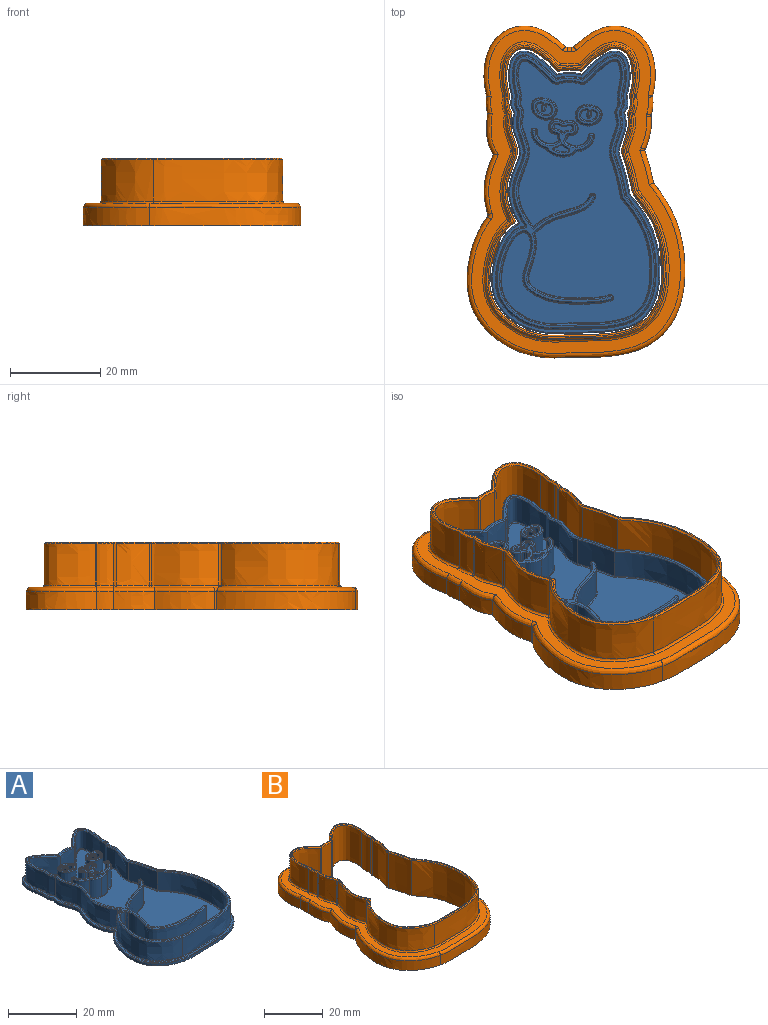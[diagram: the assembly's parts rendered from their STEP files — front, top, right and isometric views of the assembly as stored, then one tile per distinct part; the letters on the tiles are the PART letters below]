
ASSEMBLY  parts=2 mates=1
PART A: 278 faces, bbox 38x64x8.3 mm
  f0: plane 58.1x32.85mm, normal (0,0,1), area 1171.6mm2, adj f142,f143,f144,f146,f147,f148,f149,f150
  f1: plane 62.1x36.86mm, normal (0,0,1), area 109.3mm2, adj f176,f177,f178,f179,f180,f181,f182,f183
  f2: extruded ~24.09x2.39mm, area 20.1mm2, adj f9,f10,f101,f182
  f3: extruded ~23.81x10.4mm, area 24.8mm2, adj f4,f10,f101,f183
  f4: extruded ~30.82x26.84mm, area 43.2mm2, adj f3,f5,f10,f181
  f5: extruded ~8.83x2.36mm, area 7.3mm2, adj f4,f6,f10,f179
  f6: extruded ~9.18x1.59mm, area 7.6mm2, adj f5,f7,f10,f177
  f7: extruded ~13.63x10.73mm, area 19.6mm2, adj f6,f8,f10,f176
  f8: extruded ~5.46x0.8mm, area 4.4mm2, adj f7,f9,f10,f178
  f9: extruded ~13.63x10.73mm, area 19.6mm2, adj f2,f8,f10,f180
  f10: plane 62.5x37.25mm, normal (0,0,-1), area 1734.6mm2, adj f2,f3,f4,f5,f6,f7,f8,f9
  f11: extruded ~6.55x0.43mm, area 2.8mm2, adj f12,f96,f138,f214
  f12: extruded ~22.13x9.63mm, area 191.2mm2, adj f11,f13,f136,f212
  f13: extruded ~29.37x25.61mm, area 339.5mm2, adj f12,f14,f134,f210
  f14: extruded ~9.01x6.55mm, area 61.1mm2, adj f13,f15,f132,f208
  f15: extruded ~9.62x6.55mm, area 64.9mm2, adj f14,f16,f131,f206
  f16: extruded ~12.49x9.58mm, area 148.7mm2, adj f15,f17,f133,f207
  f17: extruded ~6.55x5.73mm, area 38.2mm2, adj f16,f18,f135,f209
  f18: extruded ~12.56x9.59mm, area 149mm2, adj f17,f19,f137,f211
  f19: extruded ~24.41x6.55mm, area 167.4mm2, adj f18,f36,f139,f213
  f20: extruded ~12.65x7.14mm, area 97.7mm2, adj f21,f94,f130,f199
  f21: extruded ~6.55x0.78mm, area 6.5mm2, adj f20,f22,f128,f197
  f22: extruded ~36.26x8.57mm, area 311.2mm2, adj f21,f23,f126,f195
  f23: extruded ~6.55x5.73mm, area 38.3mm2, adj f22,f24,f124,f193
  f24: extruded ~21.35x8.57mm, area 206.4mm2, adj f23,f25,f122,f191
  f25: extruded ~9.19x6.55mm, area 62.3mm2, adj f24,f26,f120,f189
  f26: extruded ~27.91x24.38mm, area 324.8mm2, adj f25,f27,f118,f187
  f27: extruded ~20.21x8.86mm, area 181.9mm2, adj f26,f28,f116,f185
  f28: extruded ~6.55x0.93mm, area 7.1mm2, adj f27,f29,f114,f186
  f29: extruded ~19.53x14.59mm, area 205mm2, adj f28,f93,f112,f188
  f30: plane 6.55x0.17mm, normal (0.64,0.77,0), area 1.4mm2, adj f92,f93,f111,f192
  f31: extruded ~18.01x14.07mm, area 194.5mm2, adj f32,f92,f115,f196
  f32: extruded ~6.55x0.13mm, area 0.9mm2, adj f31,f91,f117,f198
  f33: extruded ~6.55x0.42mm, area 3.8mm2, adj f34,f91,f121,f202
  f34: extruded ~12.92x7.56mm, area 101mm2, adj f33,f95,f123,f204
  f35: plane 6.55x0.19mm, normal (0.27,0.96,0), area 1.3mm2, adj f94,f95,f127,f203
  f36: extruded ~6.55x0.37mm, area 3mm2, adj f19,f96,f141,f215
  f37: plane 60.43x35.28mm, normal (0,0,1), area 95.6mm2, adj f110,f111,f112,f113,f114,f115,f116,f117
  f38: extruded ~6.75x1.42mm, area 20.1mm2, adj f39,f77,f80,f229
  f39: extruded ~6.75x1.1mm, area 8.2mm2, adj f38,f40,f80,f231
  f40: extruded ~6.75x0.18mm, area 1.7mm2, adj f39,f41,f80,f233
  f41: extruded ~6.75x0.25mm, area 2mm2, adj f40,f42,f80,f234
  f42: extruded ~6.75x1.03mm, area 8.2mm2, adj f41,f43,f80,f232
  f43: extruded ~6.75x1.32mm, area 18.5mm2, adj f42,f44,f80,f230
  f44: extruded ~6.75x0.51mm, area 3.7mm2, adj f43,f45,f80,f228
  f45: extruded ~6.75x0.28mm, area 1.9mm2, adj f44,f46,f80,f226
  f46: extruded ~6.75x0.24mm, area 1.6mm2, adj f45,f77,f80,f225
  f47: extruded ~6.5x3.33mm, area 29.5mm2, adj f48,f97,f172,f270
  f48: extruded ~6.5x1.96mm, area 14.8mm2, adj f47,f108,f174,f268
  f49: extruded ~6.5x0.39mm, area 2.9mm2, adj f50,f108,f173,f264
  f50: extruded ~6.5x0.44mm, area 3.1mm2, adj f49,f51,f171,f262
  f51: plane 6.5x0.02mm, normal (0.97,-0.26,0), area 0.2mm2, adj f50,f52,f169
  f52: extruded ~6.5x0.39mm, area 3.3mm2, adj f51,f53,f167,f259
  f53: extruded ~6.5x0.01mm, area 0.1mm2, adj f52,f164,f245
  f54: extruded ~6.5x0.09mm, area 0.6mm2, adj f55,f165,f245,f255
  f55: extruded ~6.5x3.08mm, area 39.8mm2, adj f54,f56,f162,f253
  f56: extruded ~6.5x0.31mm, area 2.1mm2, adj f55,f57,f160,f251
  f57: extruded ~6.5x0.34mm, area 2.3mm2, adj f56,f58,f154,f156,f158,f249
  f58: extruded ~6.5x0.47mm, area 3.4mm2, adj f57,f59,f152,f248
  f59: extruded ~6.5x3.01mm, area 35.7mm2, adj f58,f60,f150,f250
  f60: extruded ~6.5x0.48mm, area 3.2mm2, adj f59,f61,f148,f252
  f61: extruded ~6.5x0.47mm, area 3.9mm2, adj f60,f62,f146,f254
  f62: plane 6.5x0.02mm, normal (-1,-0.05,0), area 0.1mm2, adj f61,f63,f144
  f63: extruded ~6.5x0.46mm, area 3mm2, adj f62,f64,f142,f257
  f64: extruded ~6.5x0.42mm, area 2.9mm2, adj f63,f109,f143,f258
  f65: extruded ~6.5x2.11mm, area 14.8mm2, adj f66,f109,f147,f261
  f66: extruded ~6.5x2.89mm, area 29.5mm2, adj f65,f100,f149,f263
  f67: plane 6.5x0.2mm, normal (0.16,0.99,0), area 1.3mm2, adj f99,f100,f153,f267
  f68: extruded ~6.5x3.91mm, area 35.9mm2, adj f69,f99,f157,f271
  f69: extruded ~6.5x3.21mm, area 24.6mm2, adj f68,f70,f159,f273
  f70: extruded ~6.5x3.46mm, area 24.6mm2, adj f69,f71,f161,f275
  f71: extruded ~6.5x3.81mm, area 35.9mm2, adj f70,f98,f163,f277
  f72: extruded ~6.75x1.4mm, area 12mm2, adj f76,f79,f106,f222
  f73: extruded ~6.75x1.51mm, area 10.3mm2, adj f74,f79,f106,f219
  f74: extruded ~6.75x1.47mm, area 10.3mm2, adj f73,f79,f107,f221
  f75: plane 6.5x0.2mm, normal (0.02,1,0), area 1.3mm2, adj f97,f98,f168,f274
  f76: extruded ~6.75x1.56mm, area 12mm2, adj f72,f79,f107,f224
  f77: extruded ~6.75x0.41mm, area 2.8mm2, adj f38,f46,f80,f227
  f78: plane 13.32x7.75mm, normal (0,0,1), area 17.7mm2, adj f219,f220,f221,f222,f223,f224,f225,f226
  f79: plane 3.24x1.59mm, normal (0,0,1), area 2.9mm2, adj f72,f73,f74,f76,f106,f107
  f80: plane 4.21x1.97mm, normal (0,0,1), area 4.2mm2, adj f38,f39,f40,f41,f42,f43,f44,f45
  f81: extruded ~6.75x3.56mm, area 55.2mm2, adj f85,f104,f105,f241
  f82: extruded ~6.55x5.53mm, area 102.5mm2, adj f218,f244
  f83: extruded ~6.75x1.59mm, area 24.3mm2, adj f85,f104,f105,f242
  f84: plane 5.33x4.14mm, normal (0,0,1), area 7.4mm2, adj f240,f241,f242,f243,f244
  f85: plane 3.64x2.43mm, normal (0,0,1), area 5mm2, adj f81,f83,f104,f105
  f86: extruded ~6.75x3.38mm, area 55.2mm2, adj f90,f102,f103,f237
  f87: extruded ~6.75x1.63mm, area 24.3mm2, adj f90,f102,f103,f236
  f88: extruded ~6.55x5.36mm, area 102.5mm2, adj f217,f239
  f89: plane 5.11x4.28mm, normal (0,0,1), area 7.1mm2, adj f235,f236,f237,f238,f239
  f90: plane 3.46x2.64mm, normal (0,0,1), area 5mm2, adj f86,f87,f102,f103
  f91: cylinder r=0.4mm len=6.55mm, axis (0,0,-1), area 3mm2, adj f32,f33,f119,f200
  f92: cylinder r=0.4mm len=6.55mm, axis (0,0,-1), area 2.9mm2, adj f30,f31,f113,f194
  f93: cylinder r=0.4mm len=6.55mm, axis (0,0,-1), area 5.2mm2, adj f29,f30,f110,f190
  f94: cylinder r=0.4mm len=6.55mm, axis (0,0,-1), area 3.9mm2, adj f20,f35,f129,f201
  f95: cylinder r=0.4mm len=6.55mm, axis (0,0,-1), area 4.3mm2, adj f34,f35,f125,f205
  f96: cylinder r=0.4mm len=6.55mm, axis (0,0,-1), area 5.6mm2, adj f11,f36,f140,f216
  f97: cylinder r=0.4mm len=6.5mm, axis (0,0,-1), area 3.9mm2, adj f47,f75,f170,f272
  f98: cylinder r=0.4mm len=6.5mm, axis (0,0,-1), area 4.2mm2, adj f71,f75,f166,f276
  f99: cylinder r=0.4mm len=6.5mm, axis (0,0,-1), area 4.2mm2, adj f67,f68,f155,f269
  f100: cylinder r=0.4mm len=6.5mm, axis (0,0,-1), area 3.9mm2, adj f66,f67,f151,f265
  f101: cylinder r=0.4mm len=0.8mm, axis (0,0,-1), area 0.5mm2, adj f2,f3,f10,f184
  f102: cylinder r=0.2mm len=6.75mm, axis (0,0,-1), area 2.9mm2, adj f86,f87,f90,f235
  f103: cylinder r=0.2mm len=6.75mm, axis (0,0,-1), area 3mm2, adj f86,f87,f90,f238
  f104: cylinder r=0.2mm len=6.75mm, axis (0,0,-1), area 3mm2, adj f81,f83,f85,f243
  f105: cylinder r=0.2mm len=6.75mm, axis (0,0,-1), area 2.9mm2, adj f81,f83,f85,f240
  f106: cylinder r=0.2mm len=6.75mm, axis (0,0,-1), area 3.3mm2, adj f72,f73,f79,f220
  f107: cylinder r=0.2mm len=6.75mm, axis (0,0,-1), area 3.3mm2, adj f74,f76,f79,f223
  f108: cylinder r=0.2mm len=6.5mm, axis (0,0,-1), area 1.6mm2, adj f48,f49,f175,f266
  f109: cylinder r=0.2mm len=6.5mm, axis (0,0,-1), area 1.6mm2, adj f64,f65,f145,f260
  f110: cone r=0.15mm half-angle=45deg, axis (0,0,-1), area 0.2mm2, adj f37,f93,f111,f112
  f111: plane 0.33x0.33mm, normal (0.45,0.54,0.71), area 0.1mm2, adj f30,f37,f110,f113
  f112: bspline ~19.57x14.67mm, area 11mm2, adj f29,f37,f110,f114
  f113: cone r=0.15mm half-angle=45deg, axis (0,0,-1), area 0.1mm2, adj f37,f92,f111,f115
  f114: bspline ~1.11x0.76mm, area 0.4mm2, adj f28,f37,f112,f116
  f115: bspline ~18.39x14.32mm, area 10.6mm2, adj f31,f37,f113,f117
  f116: bspline ~20.73x9.13mm, area 10mm2, adj f27,f37,f114,f118
  f117: bspline ~0.28x0.25mm, area 0mm2, adj f32,f37,f115,f119
  f118: bspline ~30.2x24.71mm, area 17.6mm2, adj f26,f37,f116,f120
  f119: cone r=0.65mm half-angle=45deg, axis (0,0,1), area 0.2mm2, adj f37,f91,f117,f121
  f120: bspline ~10.19x2.93mm, area 3.4mm2, adj f25,f37,f118,f122
  f121: bspline ~0.6x0.59mm, area 0.2mm2, adj f33,f37,f119,f123
  f122: bspline ~22.56x9.76mm, area 11.2mm2, adj f24,f37,f120,f124
  f123: bspline ~13.09x7.64mm, area 5.4mm2, adj f34,f37,f121,f125
  f124: bspline ~5.88x0.76mm, area 2.1mm2, adj f23,f37,f122,f126
  f125: cone r=0.15mm half-angle=45deg, axis (0,0,-1), area 0.2mm2, adj f37,f95,f123,f127
  f126: bspline ~36.74x9.07mm, area 16.8mm2, adj f22,f37,f124,f128
  f127: plane 0.3x0.26mm, normal (0.19,0.68,0.71), area 0.1mm2, adj f35,f37,f125,f129
  f128: bspline ~1.14x1mm, area 0.4mm2, adj f21,f37,f126,f130
  f129: cone r=0.15mm half-angle=45deg, axis (0,0,-1), area 0.1mm2, adj f37,f94,f127,f130
  f130: bspline ~13.64x8.03mm, area 5.3mm2, adj f20,f37,f128,f129
  f131: bspline ~10.23x1.85mm, area 3.5mm2, adj f15,f37,f132,f133
  f132: bspline ~10.04x2.9mm, area 3.3mm2, adj f14,f37,f131,f134
  f133: bspline ~12.55x9.83mm, area 8mm2, adj f16,f37,f131,f135
  f134: bspline ~29.42x25.61mm, area 18.2mm2, adj f13,f37,f132,f136
  f135: bspline ~6.47x0.82mm, area 2.1mm2, adj f17,f37,f133,f137
  f136: bspline ~22.13x9.74mm, area 10.2mm2, adj f12,f37,f134,f138
  f137: bspline ~12.65x9.82mm, area 8.1mm2, adj f18,f37,f135,f139
  f138: bspline ~0.44x0.3mm, area 0.1mm2, adj f11,f37,f136,f140
  f139: bspline ~24.41x2.7mm, area 9mm2, adj f19,f37,f137,f141
  f140: cone r=0.65mm half-angle=45deg, axis (0,0,1), area 0.4mm2, adj f37,f96,f138,f141
  f141: bspline ~0.51x0.46mm, area 0.2mm2, adj f36,f37,f139,f140
  f142: bspline ~0.71x0.33mm, area 0.2mm2, adj f0,f63,f143,f144
  f143: bspline ~1.4x0.6mm, area 0.1mm2, adj f0,f64,f142,f145
  f144: cylinder r=0.2mm len=0.2mm, axis (-0.05,1,0), area 0mm2, adj f0,f62,f142,f146
  f145: sphere r=0.2mm, area 0.1mm2, adj f109,f143,f147
  f146: bspline ~0.64x0.48mm, area 0.2mm2, adj f0,f61,f144,f148
  f147: bspline ~3.01x0.97mm, area 0.7mm2, adj f0,f65,f145,f149
  f148: bspline ~1.53x0.58mm, area 0.2mm2, adj f0,f60,f146,f150
  f149: bspline ~4.46x3.35mm, area 1.4mm2, adj f0,f66,f147,f151
  f150: bspline ~3.61x3.52mm, area 1.8mm2, adj f0,f59,f148,f152
  f151: torus R=0.6mm, axis (0,0,1), area 0.2mm2, adj f0,f100,f149,f153
  f152: bspline ~0.95x0.59mm, area 0.2mm2, adj f0,f58,f150,f154
  f153: cylinder r=0.2mm len=0.23mm, axis (0.99,-0.16,0), area 0.1mm2, adj f0,f67,f151,f155
  f154: bspline ~0.28x0.27mm, area 0mm2, adj f0,f57,f152,f156
  f155: torus R=0.6mm, axis (0,0,1), area 0.2mm2, adj f0,f99,f153,f157
  f156: bspline ~0.2x0.2mm, area 0mm2, adj f57,f154,f158
  f157: bspline ~4.69x3.57mm, area 1.8mm2, adj f0,f68,f155,f159
  f158: bspline ~0.3x0.25mm, area 0mm2, adj f0,f57,f156,f160
  f159: bspline ~4.46x2.13mm, area 1.2mm2, adj f0,f69,f157,f161
  f160: bspline ~0.6x0.35mm, area 0.1mm2, adj f0,f56,f158,f162
  f161: bspline ~4.73x1.46mm, area 1.2mm2, adj f0,f70,f159,f163
  f162: bspline ~3.63x3.48mm, area 2mm2, adj f0,f55,f160,f165
  f163: bspline ~4.2x4.03mm, area 1.8mm2, adj f0,f71,f161,f166
  f164: bspline ~0.2x0.17mm, area 0mm2, adj f53,f167,f246
  f165: bspline ~0.2x0.2mm, area 0mm2, adj f0,f54,f162,f246,f247
  f166: torus R=0.6mm, axis (0,0,1), area 0.2mm2, adj f0,f98,f163,f168
  f167: bspline ~0.58x0.53mm, area 0.1mm2, adj f0,f52,f164,f169,f247
  f168: cylinder r=0.2mm len=0.2mm, axis (1,-0.02,0), area 0.1mm2, adj f0,f75,f166,f170
  f169: cylinder r=0.2mm len=0.2mm, axis (-0.26,-0.97,0), area 0mm2, adj f0,f51,f167,f171
  f170: torus R=0.6mm, axis (0,0,1), area 0.2mm2, adj f0,f97,f168,f172
  f171: bspline ~0.72x0.44mm, area 0.2mm2, adj f0,f50,f169,f173
  f172: bspline ~3.75x2.78mm, area 1.4mm2, adj f0,f47,f170,f174
  f173: bspline ~1.33x0.81mm, area 0.1mm2, adj f0,f49,f171,f175
  f174: bspline ~2.86x1.41mm, area 0.7mm2, adj f0,f48,f172,f175
  f175: sphere r=0.2mm, area 0mm2, adj f108,f173,f174
  f176: bspline ~13.85x10.97mm, area 7.7mm2, adj f1,f7,f177,f178
  f177: bspline ~9.52x1.79mm, area 3mm2, adj f1,f6,f176,f179
  f178: bspline ~6.2x0.68mm, area 1.8mm2, adj f1,f8,f176,f180
  f179: bspline ~10.65x3.01mm, area 2.9mm2, adj f1,f5,f177,f181
  f180: bspline ~13.81x11.09mm, area 7.7mm2, adj f1,f9,f178,f182
  f181: bspline ~37.66x31.17mm, area 16.9mm2, adj f1,f4,f179,f183
  f182: bspline ~26.76x2.64mm, area 7.9mm2, adj f1,f2,f180,f184
  f183: bspline ~25.35x16.73mm, area 9.7mm2, adj f1,f3,f181,f184
  f184: torus R=0.6mm, axis (0,0,1), area 0.3mm2, adj f1,f101,f182,f183
  f185: bspline ~21.49x14.27mm, area 8.6mm2, adj f0,f27,f186,f187
  f186: bspline ~1.25x0.76mm, area 0.3mm2, adj f0,f28,f185,f188
  f187: bspline ~33.64x28.16mm, area 15.5mm2, adj f0,f26,f185,f189
  f188: bspline ~20.06x18.6mm, area 9.9mm2, adj f0,f29,f186,f190
  f189: bspline ~12.46x3.71mm, area 3mm2, adj f0,f25,f187,f191
  f190: torus R=0.6mm, axis (0,0,1), area 0.3mm2, adj f0,f93,f188,f192
  f191: bspline ~21.67x8.87mm, area 9.9mm2, adj f0,f24,f189,f193
  f192: cylinder r=0.2mm len=0.3mm, axis (0.77,-0.64,0), area 0.1mm2, adj f0,f30,f190,f194
  f193: bspline ~6.81x0.95mm, area 1.8mm2, adj f0,f23,f191,f195
  f194: torus R=0.6mm, axis (0,0,1), area 0.2mm2, adj f0,f92,f192,f196
  f195: bspline ~56.12x18.18mm, area 14.9mm2, adj f0,f22,f193,f197
  f196: bspline ~25.29x20.52mm, area 9.3mm2, adj f0,f31,f194,f198
  f197: bspline ~1.21x1.04mm, area 0.3mm2, adj f0,f21,f195,f199
  f198: bspline ~0.28x0.27mm, area 0mm2, adj f0,f32,f196,f200
  f199: bspline ~13.33x7.9mm, area 4.6mm2, adj f0,f20,f197,f201
  f200: torus R=0.2mm, axis (0,0,1), area 0.1mm2, adj f0,f91,f198,f202
  f201: torus R=0.6mm, axis (0,0,1), area 0.2mm2, adj f0,f94,f199,f203
  f202: bspline ~0.69x0.67mm, area 0.2mm2, adj f0,f33,f200,f204
  f203: cylinder r=0.2mm len=0.25mm, axis (0.96,-0.27,0), area 0.1mm2, adj f0,f35,f201,f205
  f204: bspline ~13.95x8.77mm, area 4.9mm2, adj f0,f34,f202,f205
  f205: torus R=0.6mm, axis (0,0,1), area 0.2mm2, adj f0,f95,f203,f204
  f206: bspline ~9.92x1.8mm, area 3.1mm2, adj f1,f15,f207,f208
  f207: bspline ~13.93x10.04mm, area 7.2mm2, adj f1,f16,f206,f209
  f208: bspline ~10.76x3.04mm, area 2.9mm2, adj f1,f14,f206,f210
  f209: bspline ~6.34x0.75mm, area 1.8mm2, adj f1,f17,f207,f211
  f210: bspline ~35.38x30mm, area 16.3mm2, adj f1,f13,f208,f212
  f211: bspline ~14.71x9.99mm, area 7.3mm2, adj f1,f18,f209,f213
  f212: bspline ~24.59x15.47mm, area 9.2mm2, adj f1,f12,f210,f214
  f213: bspline ~34.58x9.09mm, area 8mm2, adj f1,f19,f211,f215
  f214: bspline ~1.66x0.45mm, area 0.1mm2, adj f1,f11,f212,f216
  f215: bspline ~0.62x0.51mm, area 0.1mm2, adj f1,f36,f213,f216
  f216: torus R=0.2mm, axis (0,0,1), area 0.2mm2, adj f1,f96,f214,f215
  f217: bspline ~5.79x4.98mm, area 5.1mm2, adj f0,f88
  f218: bspline ~5.97x4.78mm, area 5.1mm2, adj f0,f82
  f219: bspline ~1.6x0.43mm, area 0.6mm2, adj f73,f78,f220,f221
  f220: cone r=0.45mm half-angle=45deg, axis (0,0,1), area 0.3mm2, adj f78,f106,f219,f222
  f221: bspline ~1.58x0.65mm, area 0.6mm2, adj f74,f78,f219,f223
  f222: bspline ~1.67x1.41mm, area 0.7mm2, adj f72,f78,f220,f224
  f223: cone r=0.45mm half-angle=45deg, axis (0,0,1), area 0.3mm2, adj f78,f107,f221,f224
  f224: bspline ~1.82x1.15mm, area 0.7mm2, adj f76,f78,f222,f223
  f225: bspline ~0.29x0.28mm, area 0.1mm2, adj f46,f78,f226,f227
  f226: bspline ~0.34x0.27mm, area 0.1mm2, adj f45,f78,f225,f228
  f227: bspline ~0.41x0.31mm, area 0.1mm2, adj f77,f78,f225,f229
  f228: bspline ~0.56x0.44mm, area 0.2mm2, adj f44,f78,f226,f230
  f229: bspline ~1.74x1.58mm, area 1.2mm2, adj f38,f78,f227,f231
  f230: bspline ~1.68x1.62mm, area 1.1mm2, adj f43,f78,f228,f232
  f231: bspline ~1.1x0.61mm, area 0.4mm2, adj f39,f78,f229,f233
  f232: bspline ~1.08x0.73mm, area 0.4mm2, adj f42,f78,f230,f234
  f233: bspline ~0.59x0.57mm, area 0.1mm2, adj f40,f78,f231,f234
  f234: bspline ~0.69x0.56mm, area 0.2mm2, adj f41,f78,f232,f233
  f235: cone r=0.45mm half-angle=45deg, axis (0,0,1), area 0.2mm2, adj f89,f102,f236,f237
  f236: bspline ~1.63x1.09mm, area 1.1mm2, adj f87,f89,f235,f238
  f237: bspline ~3.94x3.12mm, area 3.1mm2, adj f86,f89,f235,f238
  f238: cone r=0.45mm half-angle=45deg, axis (0,0,1), area 0.3mm2, adj f89,f103,f236,f237
  f239: bspline ~5.5x4.6mm, area 5.3mm2, adj f88,f89
  f240: cone r=0.45mm half-angle=45deg, axis (0,0,1), area 0.2mm2, adj f84,f105,f241,f242
  f241: bspline ~4.1x2.89mm, area 3.1mm2, adj f81,f84,f240,f243
  f242: bspline ~1.59x1.11mm, area 1.1mm2, adj f83,f84,f240,f243
  f243: cone r=0.45mm half-angle=45deg, axis (0,0,1), area 0.3mm2, adj f84,f104,f241,f242
  f244: bspline ~5.55x4.37mm, area 5.3mm2, adj f82,f84
  f245: cylinder r=0.05mm len=6.5mm, axis (0,0,-1), area 0.2mm2, adj f53,f54,f246
  f246: bspline ~0.16x0.07mm, area 0mm2, adj f164,f165,f245,f247
  f247: bspline ~0.19x0.12mm, area 0mm2, adj f165,f167,f246
  f248: bspline ~0.62x0.52mm, area 0.2mm2, adj f58,f78,f249,f250
  f249: bspline ~0.67x0.42mm, area 0.2mm2, adj f57,f78,f248,f251
  f250: bspline ~3.06x2.64mm, area 2.1mm2, adj f59,f78,f248,f252
  f251: bspline ~0.41x0.39mm, area 0.1mm2, adj f56,f78,f249,f253
  f252: bspline ~0.6x0.4mm, area 0.2mm2, adj f60,f78,f250,f254
  f253: bspline ~3.16x2.52mm, area 2.4mm2, adj f55,f78,f251,f255
  f254: bspline ~0.78x0.64mm, area 0.3mm2, adj f61,f78,f252,f257
  f255: bspline ~0.3x0.3mm, area 0mm2, adj f54,f78,f253,f256
  f256: cone r=0.35mm half-angle=45deg, axis (0,0,1), area 0.1mm2, adj f78,f255,f259
  f257: bspline ~0.51x0.38mm, area 0.2mm2, adj f63,f78,f254,f258
  f258: bspline ~0.5x0.42mm, area 0.2mm2, adj f64,f78,f257,f260
  f259: bspline ~0.68x0.6mm, area 0.3mm2, adj f52,f78,f256,f262
  f260: cone r=0.5mm half-angle=45deg, axis (0,0,1), area 0.2mm2, adj f78,f109,f258,f261
  f261: bspline ~2.32x1.02mm, area 1mm2, adj f65,f78,f260,f263
  f262: bspline ~0.52x0.44mm, area 0.2mm2, adj f50,f78,f259,f264
  f263: bspline ~3.22x3.21mm, area 2mm2, adj f66,f78,f261,f265
  f264: bspline ~0.52x0.47mm, area 0.2mm2, adj f49,f78,f262,f266
  f265: cone r=0.1mm half-angle=45deg, axis (0,0,-1), area 0.2mm2, adj f78,f100,f263,f267
  f266: cone r=0.5mm half-angle=45deg, axis (0,0,1), area 0.2mm2, adj f78,f108,f264,f268
  f267: plane 0.33x0.3mm, normal (0.11,0.7,0.71), area 0.1mm2, adj f67,f78,f265,f269
  f268: bspline ~2.19x1.33mm, area 1mm2, adj f48,f78,f266,f270
  f269: cone r=0.1mm half-angle=45deg, axis (0,0,-1), area 0.2mm2, adj f78,f99,f267,f271
  f270: bspline ~3.67x2.69mm, area 2mm2, adj f47,f78,f268,f272
  f271: bspline ~3.94x3.39mm, area 2.3mm2, adj f68,f78,f269,f273
  f272: cone r=0.1mm half-angle=45deg, axis (0,0,-1), area 0.2mm2, adj f78,f97,f270,f274
  f273: bspline ~3.31x2mm, area 1.6mm2, adj f69,f78,f271,f275
  f274: plane 0.3x0.3mm, normal (0.01,0.71,0.71), area 0.1mm2, adj f75,f78,f272,f276
  f275: bspline ~3.55x1.47mm, area 1.6mm2, adj f70,f78,f273,f277
  f276: cone r=0.1mm half-angle=45deg, axis (0,0,-1), area 0.2mm2, adj f78,f98,f274,f277
  f277: bspline ~3.95x3.33mm, area 2.3mm2, adj f71,f78,f275,f276
PART B: 130 faces, bbox 50.9x74.7x15.5 mm
  f0: extruded ~9.16x8.53mm, area 81.1mm2, adj f1,f24,f72,f111
  f1: extruded ~32.99x28.69mm, area 525.7mm2, adj f0,f2,f73,f109
  f2: extruded ~25.82x11.55mm, area 304.1mm2, adj f1,f48,f75,f108
  f3: extruded ~14.82x9.16mm, area 141.5mm2, adj f25,f48,f79,f112
  f4: extruded ~9.16x7.46mm, area 70.6mm2, adj f5,f25,f82,f116
  f5: extruded ~9.16x0.54mm, area 5.1mm2, adj f4,f6,f84,f118
  f6: extruded ~9.16x3.74mm, area 35.3mm2, adj f5,f7,f86,f119
  f7: plane 9.16x0.2mm, normal (-0.99,0.14,0), area 1.8mm2, adj f6,f8,f88,f121
  f8: extruded ~12.5x11.43mm, area 211.7mm2, adj f7,f49,f90,f123
  f9: extruded ~9.16x3.98mm, area 36.6mm2, adj f49,f50,f87,f124
  f10: extruded ~12.5x11.42mm, area 211.4mm2, adj f11,f50,f83,f120,f129
  f11: extruded ~9.16x0.05mm, area 0.5mm2, adj f10,f51,f81,f128
  f12: extruded ~14.66x1.39mm, area 21.9mm2, adj f13,f28,f55,f70
  f13: extruded ~14.66x4.76mm, area 70.8mm2, adj f12,f14,f28,f71
  f14: extruded ~14.66x11.15mm, area 278.5mm2, adj f13,f28,f52,f69
  f15: extruded ~14.66x4.65mm, area 68.7mm2, adj f28,f52,f53,f65
  f16: extruded ~14.66x11.15mm, area 311.8mm2, adj f17,f28,f53,f61
  f17: extruded ~14.66x0.32mm, area 4.7mm2, adj f16,f18,f28,f59
  f18: extruded ~14.66x3.46mm, area 52.7mm2, adj f17,f19,f28,f57
  f19: extruded ~23.73x14.66mm, area 362.2mm2, adj f18,f28,f54,f56
  f20: extruded ~24.48x14.66mm, area 464.2mm2, adj f21,f28,f54,f60
  f21: extruded ~31.54x27.46mm, area 808.7mm2, adj f20,f22,f28,f62
  f22: extruded ~14.66x8.73mm, area 132.7mm2, adj f21,f26,f28,f64
  f23: extruded ~9.16x3.73mm, area 35.1mm2, adj f47,f51,f78,f117,f126
  f24: extruded ~9.16x8.4mm, area 79.2mm2, adj f0,f47,f74,f113
  f25: extruded ~9.16x0.45mm, area 4.1mm2, adj f3,f4,f80,f114
  f26: extruded ~14.66x8.78mm, area 132.4mm2, adj f22,f28,f55,f66
  f27: plane 65.33x40.2mm, normal (0,0,1), area 57mm2, adj f56,f57,f58,f59,f60,f61,f62,f63
  f28: plane 73.5x48.25mm, normal (0,0,-1), area 1013.8mm2, adj f12,f13,f14,f15,f16,f17,f18,f19
  f29: extruded ~4.09x4mm, area 16.6mm2, adj f28,f42,f46,f96
  f30: extruded ~7.32x4mm, area 30.1mm2, adj f28,f31,f42,f92
  f31: extruded ~4x0.29mm, area 1.2mm2, adj f28,f30,f32,f91
  f32: extruded ~7.16x4mm, area 29.7mm2, adj f28,f31,f33,f93
  f33: extruded ~38.75x33.63mm, area 265.3mm2, adj f28,f32,f34,f95
  f34: extruded ~30.75x14.61mm, area 156.4mm2, adj f28,f33,f43,f97
  f35: extruded ~13.25x4mm, area 54.6mm2, adj f28,f36,f43,f101
  f36: extruded ~9.08x4mm, area 37.4mm2, adj f28,f35,f37,f103
  f37: extruded ~4x3.89mm, area 15.7mm2, adj f28,f36,f38,f105
  f38: extruded ~18.07x15.57mm, area 123.4mm2, adj f28,f37,f44,f107
  f39: extruded ~4x1.05mm, area 4.2mm2, adj f28,f44,f45,f104
  f40: extruded ~18.07x15.48mm, area 122.8mm2, adj f28,f45,f46,f100
  f41: plane 71.55x46.31mm, normal (0,0,1), area 512.6mm2, adj f91,f92,f93,f94,f95,f96,f97,f98
  f42: cylinder r=0.5mm len=4mm, axis (0,0,-1), area 0.9mm2, adj f28,f29,f30,f94
  f43: cylinder r=0.5mm len=4mm, axis (0,0,-1), area 2mm2, adj f28,f34,f35,f99
  f44: cylinder r=0.5mm len=4mm, axis (0,0,-1), area 1.6mm2, adj f28,f38,f39,f106
  f45: cylinder r=0.5mm len=4mm, axis (0,0,-1), area 1.6mm2, adj f28,f39,f40,f102
  f46: cylinder r=0.5mm len=4mm, axis (0,0,-1), area 0.7mm2, adj f28,f29,f40,f98
  f47: cylinder r=0.5mm len=9.16mm, axis (0,0,-1), area 3.1mm2, adj f23,f24,f76,f115
  f48: cylinder r=0.5mm len=9.16mm, axis (0,0,-1), area 6.3mm2, adj f2,f3,f77,f110
  f49: cylinder r=0.5mm len=9.16mm, axis (0,0,-1), area 4.7mm2, adj f8,f9,f89,f125
  f50: cylinder r=0.5mm len=9.16mm, axis (0,0,-1), area 4.7mm2, adj f9,f10,f85,f122
  f51: cylinder r=0.5mm len=9.16mm, axis (0,0,-1), area 0.2mm2, adj f11,f23,f127
  f52: cylinder r=0.5mm len=14.66mm, axis (0,0,-1), area 7.7mm2, adj f14,f15,f28,f67
  f53: cylinder r=0.5mm len=14.66mm, axis (0,0,-1), area 7.7mm2, adj f15,f16,f28,f63
  f54: cylinder r=0.5mm len=14.66mm, axis (0,0,-1), area 11.3mm2, adj f19,f20,f28,f58
  f55: cylinder r=0.5mm len=14.66mm, axis (0,0,-1), area 5.4mm2, adj f12,f26,f28,f68
  f56: bspline ~25.16x2.78mm, area 11.9mm2, adj f19,f27,f57,f58
  f57: bspline ~3.68x1.01mm, area 1.7mm2, adj f18,f27,f56,f59
  f58: cone r=0.16mm half-angle=45deg, axis (0,0,-1), area 0.2mm2, adj f27,f54,f56,f60
  f59: bspline ~0.38x0.34mm, area 0.1mm2, adj f17,f27,f57,f61
  f60: bspline ~25.11x11.13mm, area 15.4mm2, adj f20,f27,f58,f62
  f61: bspline ~11.75x10.92mm, area 10.5mm2, adj f16,f27,f59,f63
  f62: bspline ~34.25x27.89mm, area 26.7mm2, adj f21,f27,f60,f64
  f63: cone r=0.16mm half-angle=45deg, axis (0,0,-1), area 0.2mm2, adj f27,f53,f61,f65
  f64: bspline ~9.73x2.92mm, area 4.3mm2, adj f22,f27,f62,f66
  f65: bspline ~4.8x0.69mm, area 2.3mm2, adj f15,f27,f63,f67
  f66: bspline ~8.85x1.93mm, area 4.3mm2, adj f26,f27,f64,f68
  f67: cone r=0.16mm half-angle=45deg, axis (0,0,-1), area 0.2mm2, adj f27,f52,f65,f69
  f68: cone r=0.16mm half-angle=45deg, axis (0,0,-1), area 0.1mm2, adj f27,f55,f66,f70
  f69: bspline ~11.77x8.41mm, area 9.3mm2, adj f14,f27,f67,f71
  f70: bspline ~1.55x0.86mm, area 0.7mm2, adj f12,f27,f68,f71
  f71: bspline ~5.07x0.87mm, area 2.3mm2, adj f13,f27,f69,f70
  f72: bspline ~8.74x2.65mm, area 4.3mm2, adj f0,f27,f73,f74
  f73: bspline ~33.06x28.69mm, area 27.4mm2, adj f1,f27,f72,f75
  f74: bspline ~8.9x1.98mm, area 4.2mm2, adj f24,f27,f72,f76
  f75: bspline ~25.82x11.68mm, area 15.8mm2, adj f2,f27,f73,f77
  f76: cone r=0.84mm half-angle=45deg, axis (0,0,1), area 0.2mm2, adj f27,f47,f74,f78
  f77: cone r=0.84mm half-angle=45deg, axis (0,0,1), area 0.4mm2, adj f27,f48,f75,f79
  f78: bspline ~3.75x0.84mm, area 1.8mm2, adj f23,f27,f76,f81
  f79: bspline ~14.82x2.82mm, area 7.4mm2, adj f3,f27,f77,f80
  f80: bspline ~0.52x0.38mm, area 0.2mm2, adj f25,f27,f79,f82
  f81: bspline ~0.34x0.34mm, area 0.1mm2, adj f11,f27,f78,f83
  f82: bspline ~7.46x1.92mm, area 3.7mm2, adj f4,f27,f80,f84
  f83: bspline ~12.51x11.59mm, area 11mm2, adj f10,f27,f81,f85
  f84: bspline ~0.76x0.48mm, area 0.3mm2, adj f5,f27,f82,f86
  f85: cone r=0.84mm half-angle=45deg, axis (0,0,1), area 0.3mm2, adj f27,f50,f83,f87
  f86: bspline ~4.21x1.08mm, area 1.8mm2, adj f6,f27,f84,f88
  f87: bspline ~3.98x0.56mm, area 1.9mm2, adj f9,f27,f85,f89
  f88: plane 0.37x0.34mm, normal (-0.7,0.1,0.71), area 0.1mm2, adj f7,f27,f86,f90
  f89: cone r=0.84mm half-angle=45deg, axis (0,0,1), area 0.3mm2, adj f27,f49,f87,f90
  f90: bspline ~12.51x11.65mm, area 11mm2, adj f8,f27,f88,f89
  f91: bspline ~1.24x1.2mm, area 0.8mm2, adj f31,f41,f92,f93
  f92: bspline ~8.21x2.59mm, area 11.5mm2, adj f30,f41,f91,f94
  f93: bspline ~14.72x5.19mm, area 12mm2, adj f32,f41,f91,f95
  f94: torus R=1.5mm, axis (0,0,-1), area 0.6mm2, adj f41,f42,f92,f96
  f95: bspline ~50.47x39.18mm, area 103.1mm2, adj f33,f41,f93,f97
  f96: bspline ~4.91x1.47mm, area 6.2mm2, adj f29,f41,f94,f98
  f97: bspline ~32.42x20.04mm, area 60.3mm2, adj f34,f41,f95,f99
  f98: torus R=1.5mm, axis (0,0,-1), area 0.5mm2, adj f41,f46,f96,f100
  f99: torus R=1.5mm, axis (0,0,-1), area 1.3mm2, adj f41,f43,f97,f101
  f100: bspline ~18.52x18.45mm, area 47.1mm2, adj f40,f41,f98,f102
  f101: bspline ~15.41x3.61mm, area 21.4mm2, adj f35,f41,f99,f103
  f102: torus R=1.5mm, axis (0,0,-1), area 1.1mm2, adj f41,f45,f100,f104
  f103: bspline ~16.57x5.54mm, area 14.9mm2, adj f36,f41,f101,f105
  f104: bspline ~1.6x1.02mm, area 1.6mm2, adj f39,f41,f102,f106
  f105: bspline ~4.73x1.46mm, area 6.3mm2, adj f37,f41,f103,f107
  f106: torus R=1.5mm, axis (0,0,-1), area 1.1mm2, adj f41,f44,f104,f107
  f107: bspline ~18.63x16.33mm, area 47.4mm2, adj f38,f41,f105,f106
  f108: bspline ~27.28x14.12mm, area 26.4mm2, adj f2,f41,f109,f110
  f109: bspline ~41.67x34.49mm, area 45.4mm2, adj f1,f41,f108,f111
  f110: sphere r=0.5mm, area 0.3mm2, adj f48,f108,f112
  f111: bspline ~9.73x3.04mm, area 6.9mm2, adj f0,f41,f109,f113
  f112: bspline ~16.19x2.93mm, area 12.2mm2, adj f3,f41,f110,f114
  f113: bspline ~9.15x2.1mm, area 6.8mm2, adj f24,f41,f111,f115
  f114: bspline ~0.55x0.54mm, area 0.3mm2, adj f25,f41,f112,f116
  f115: sphere r=0.5mm, area 0.2mm2, adj f47,f113,f117
  f116: bspline ~10.97x2.24mm, area 6.1mm2, adj f4,f41,f114,f118
  f117: bspline ~4.17x1.17mm, area 2.9mm2, adj f23,f41,f115,f126
  f118: bspline ~0.83x0.64mm, area 0.4mm2, adj f5,f41,f116,f119
  f119: bspline ~4.52x1.17mm, area 3mm2, adj f6,f41,f118,f121
  f120: bspline ~14.34x11.93mm, area 18.4mm2, adj f10,f41,f122,f129
  f121: cylinder r=0.5mm len=0.52mm, axis (0.14,0.99,0), area 0.1mm2, adj f7,f41,f119,f123
  f122: sphere r=0.5mm, area 0.3mm2, adj f50,f120,f124
  f123: bspline ~13.62x12.2mm, area 18.6mm2, adj f8,f41,f121,f125
  f124: bspline ~5.15x0.76mm, area 3.2mm2, adj f9,f41,f122,f125
  f125: sphere r=0.5mm, area 0.3mm2, adj f49,f123,f124
  f126: bspline ~0.53x0.5mm, area 0.2mm2, adj f23,f41,f117,f127
  f127: bspline ~0.5x0.5mm, area 0mm2, adj f41,f51,f126,f128
  f128: bspline ~0.5x0.5mm, area 0mm2, adj f11,f41,f127,f129
  f129: bspline ~0.54x0.5mm, area 0.2mm2, adj f10,f41,f120,f128
PLACE A t=(-12.46,-18.34,5.51)mm
PLACE B t=(-12.41,-18.27,5.51)mm
MATE fastened A.f10 <-> B.f28  axis (0,0,-1) through (-11.55,-0.05,5.51)mm
